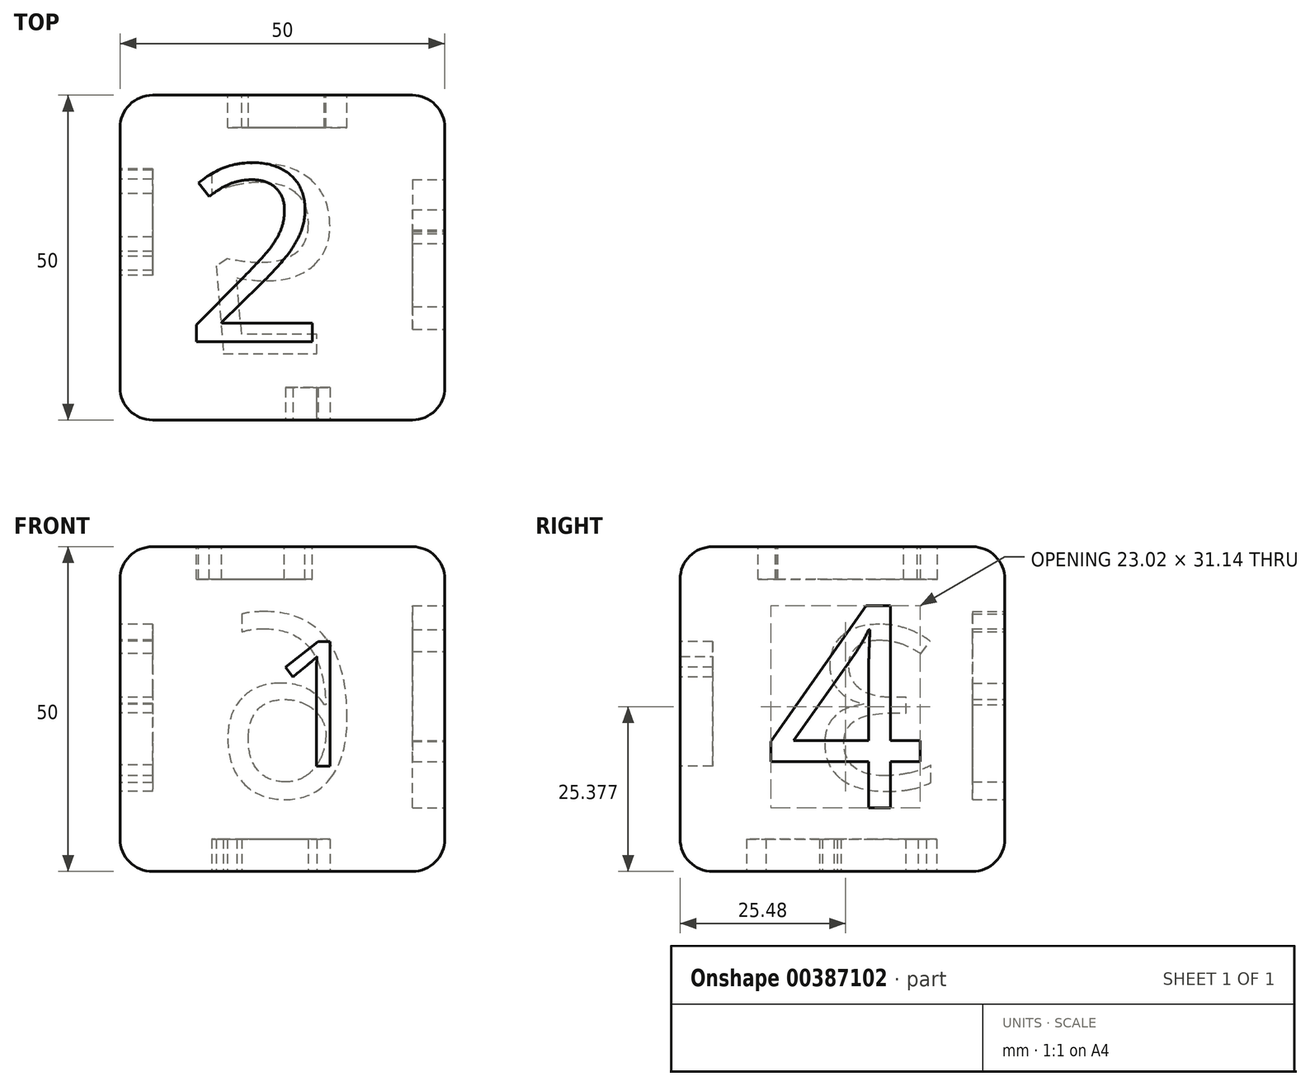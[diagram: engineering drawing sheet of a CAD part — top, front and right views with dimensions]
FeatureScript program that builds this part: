
annotation { "Feature Type Name" : "Feature", "Feature Type Description" : "" }
export const myFeature = defineFeature(function(context is Context, id is Id, definition is map)
    precondition{}
    {
        {
            var Q0;
            Q0=qCreatedBy(makeId("Front.planeOp"),FACE);
            var sketch = newSketch(context, id + "F0", { "sketchPlane" : qUnion([Q0])});
            skLineSegment(sketch, "E0.bottom", {"start": v(-34.08, 35.65) * mm, "end": v(15.92, 35.65) * mm});
            skLineSegment(sketch, "E0.top", {"start": v(-34.08, -14.35) * mm, "end": v(15.92, -14.35) * mm});
            skLineSegment(sketch, "E0.left", {"start": v(-34.08, 35.65) * mm, "end": v(-34.08, -14.35) * mm});
            skLineSegment(sketch, "E0.right", {"start": v(15.92, 35.65) * mm, "end": v(15.92, -14.35) * mm});
            skSolve(sketch);
        }
        {
            var Q0;
            Q0=makeQuery(id+"F0.imprint","IMPRINT",FACE,{"disambiguationData":[TD([[makeQuery(id+"F0.imprint","IMPRINT",EDGE,{"derivedFrom":sQuery(id+"F0.wireOp",EDGE,"E0.bottom")}),-1.0]])]});
            extrude(context, id + "F1", {"entities" : qUnion([Q0]), "depth" : 50 * mm});
        }
        {
            var Q0;
            Q0=makeQuery(id+"F1.opExtrude","CAP_FACE",FACE,{"disambiguationData":[OSD([sQuery(id+"F0.wireOp",EDGE,"E0.bottom"),sQuery(id+"F0.wireOp",EDGE,"E0.top"),sQuery(id+"F0.wireOp",EDGE,"E0.left"),sQuery(id+"F0.wireOp",EDGE,"E0.right")])],"isStart":false});
            var Q1;
            Q1=makeQuery(id+"F1.opExtrude","SWEPT_FACE",FACE,{"disambiguationData":[OSD([sQuery(id+"F0.wireOp",EDGE,"E0.right")])]});
            var Q2;
            Q2=makeQuery(id+"F1.opExtrude","CAP_EDGE",EDGE,{"disambiguationData":[OSD([sQuery(id+"F0.wireOp",EDGE,"E0.right")])],"isStart":true});
            var Q3;
            Q3=makeQuery(id+"F1.opExtrude","SWEPT_FACE",FACE,{"disambiguationData":[OSD([sQuery(id+"F0.wireOp",EDGE,"E0.bottom")])]});
            var Q4;
            Q4=makeQuery(id+"F1.opExtrude","CAP_FACE",FACE,{"disambiguationData":[OSD([sQuery(id+"F0.wireOp",EDGE,"E0.bottom"),sQuery(id+"F0.wireOp",EDGE,"E0.top"),sQuery(id+"F0.wireOp",EDGE,"E0.left"),sQuery(id+"F0.wireOp",EDGE,"E0.right")])],"isStart":true});
            var Q5;
            Q5=makeQuery(id+"F1.opExtrude","SWEPT_FACE",FACE,{"disambiguationData":[OSD([sQuery(id+"F0.wireOp",EDGE,"E0.left")])]});
            var Q6;
            Q6=makeQuery(id+"F1.opExtrude","SWEPT_FACE",FACE,{"disambiguationData":[OSD([sQuery(id+"F0.wireOp",EDGE,"E0.top")])]});
            fillet(context, id + "F2", {"entities" : qUnion([Q0, Q1, Q2, Q3, Q4, Q5, Q6]), "radius" : 5 * mm, "tangentPropagation" : true, "allowEdgeOverflow" : false});
        }
        {
            var Q0;
            Q0=makeQuery(id+"F1.opExtrude","CAP_FACE",FACE,{"disambiguationData":[OSD([sQuery(id+"F0.wireOp",EDGE,"E0.bottom"),sQuery(id+"F0.wireOp",EDGE,"E0.top"),sQuery(id+"F0.wireOp",EDGE,"E0.left"),sQuery(id+"F0.wireOp",EDGE,"E0.right")])],"isStart":false});
            var sketch = newSketch(context, id + "F3", { "sketchPlane" : qUnion([Q0])});
            skText(sketch, "E1", { "text": "1", "fontName": "OpenSans-Regular.ttf"});
            const initialGuessF3  = {"E1": [-0.0111, 0.00188, 1, 0, 0.0193]};
            skSetInitialGuess(sketch, initialGuessF3);
            skSolve(sketch);
        }
        {
            var Q0;
            Q0=qSketchRegion(id+"F3",true);
            extrude(context, id + "F4", {"entities" : qUnion([Q0]), "operationType" : NewBodyOperationType.REMOVE, "oppositeDirection" : true, "depth" : 5 * mm});
        }
        {
            var Q0;
            Q0=makeQuery(id+"F1.opExtrude","CAP_FACE",FACE,{"disambiguationData":[OSD([sQuery(id+"F0.wireOp",EDGE,"E0.bottom"),sQuery(id+"F0.wireOp",EDGE,"E0.top"),sQuery(id+"F0.wireOp",EDGE,"E0.left"),sQuery(id+"F0.wireOp",EDGE,"E0.right")])],"isStart":true});
            var sketch = newSketch(context, id + "F5", { "sketchPlane" : qUnion([Q0])});
            skText(sketch, "E2", { "text": "6", "fontName": "OpenSans-Regular.ttf"});
            const initialGuessF5  = {"E2": [-0.00313, -0.00289, 1, 0, 0.02839]};
            skSetInitialGuess(sketch, initialGuessF5);
            skSolve(sketch);
        }
        {
            var Q0;
            Q0=qSketchRegion(id+"F5",true);
            extrude(context, id + "F6", {"entities" : qUnion([Q0]), "operationType" : NewBodyOperationType.REMOVE, "oppositeDirection" : true, "depth" : 5 * mm});
        }
        {
            var Q0;
            Q0=makeQuery(id+"F1.opExtrude","SWEPT_FACE",FACE,{"disambiguationData":[OSD([sQuery(id+"F0.wireOp",EDGE,"E0.bottom")])]});
            var sketch = newSketch(context, id + "F7", { "sketchPlane" : qUnion([Q0])});
            skText(sketch, "E3", { "text": "2", "fontName": "OpenSans-Regular.ttf"});
            const initialGuessF7  = {"E3": [-0.0242, -0.03797, 1, 0, 0.02745]};
            skSetInitialGuess(sketch, initialGuessF7);
            skSolve(sketch);
        }
        {
            var Q0;
            Q0=qSketchRegion(id+"F7",true);
            extrude(context, id + "F8", {"entities" : qUnion([Q0]), "operationType" : NewBodyOperationType.REMOVE, "oppositeDirection" : true, "depth" : 5 * mm});
        }
        {
            var Q0;
            Q0=makeQuery(id+"F1.opExtrude","SWEPT_FACE",FACE,{"disambiguationData":[OSD([sQuery(id+"F0.wireOp",EDGE,"E0.top")])]});
            var sketch = newSketch(context, id + "F9", { "sketchPlane" : qUnion([Q0])});
            skText(sketch, "E4", { "text": "5", "fontName": "OpenSans-Regular.ttf"});
            const initialGuessF9  = {"E4": [-0.02258, 0.01092, 1, 0, 0.02913]};
            skSetInitialGuess(sketch, initialGuessF9);
            skSolve(sketch);
        }
        {
            var Q0;
            Q0=qSketchRegion(id+"F9",true);
            extrude(context, id + "F10", {"entities" : qUnion([Q0]), "operationType" : NewBodyOperationType.REMOVE, "oppositeDirection" : true, "depth" : 5 * mm});
        }
        {
            var Q0;
            Q0=makeQuery(id+"F1.opExtrude","SWEPT_FACE",FACE,{"disambiguationData":[OSD([sQuery(id+"F0.wireOp",EDGE,"E0.left")])]});
            var sketch = newSketch(context, id + "F11", { "sketchPlane" : qUnion([Q0])});
            skText(sketch, "E5", { "text": "3", "fontName": "OpenSans-Regular.ttf"});
            const initialGuessF11  = {"E5": [0.00975, -0.00167, 1, 0, 0.02523]};
            skSetInitialGuess(sketch, initialGuessF11);
            skSolve(sketch);
        }
        {
            var Q0;
            Q0=qSketchRegion(id+"F11",true);
            extrude(context, id + "F12", {"entities" : qUnion([Q0]), "operationType" : NewBodyOperationType.REMOVE, "oppositeDirection" : true, "depth" : 5 * mm});
        }
        {
            var Q0;
            Q0=makeQuery(id+"F1.opExtrude","SWEPT_FACE",FACE,{"disambiguationData":[OSD([sQuery(id+"F0.wireOp",EDGE,"E0.right")])]});
            var sketch = newSketch(context, id + "F13", { "sketchPlane" : qUnion([Q0])});
            skText(sketch, "E6", { "text": "4", "fontName": "OpenSans-Regular.ttf"});
            const initialGuessF13  = {"E6": [-0.03694, -0.00454, 1, 0, 0.03123]};
            skSetInitialGuess(sketch, initialGuessF13);
            skSolve(sketch);
        }
        {
            var Q0;
            Q0=qSketchRegion(id+"F13",true);
            extrude(context, id + "F14", {"entities" : qUnion([Q0]), "operationType" : NewBodyOperationType.REMOVE, "oppositeDirection" : true, "depth" : 5 * mm});
        }
    });
